# Revit family: Comfort-Height-WC-P-Round-With-Madison-Flushed-Lid-Tank-1
name_source: partatom
category: Plumbing Fixtures
units: mm (PartAtom-declared; Revit-internal decimal feet)

## family parameters
Always vertical = Yes
Cut with Voids When Loaded = No
OmniClass Number = 23.45.00.00
OmniClass Title = Sanitary, Laundry, and Cleaning Equipment
Part Type = Normal
Room Calculation Point = No
Round Connector Dimension = Use Diameter
Shared = No
Work Plane-Based = No

## types (2) — shared parameters
Flush rate = 3/6 L
Flush system/ Function = Siphon-jet Dual Flush system
Inlet Size = 13 mm
Manufacturer = HÄFELE (Thailand) Limited
Material = Ceramic White
Product Type = Two piece toilet
Product shape = Elongated
Seat cover info. = PP Soft Close System
Series = CIRINO
Standard/ code = TIS 792 : 2554
Trapway type = S-Trap rough-in 305 mm
URL = https://www.hafelethailand.com
zero-valued in all types: Default Elevation

## per-type parameters (varying)
| type | Height | Length | Outlet Size | Product code | SKU-1 | SKU-2 | Weight | Width |
| HAFELE Two piece toilet CIRINO 588.51.421 | 787 mm  [stored 2.58202 ft] | 766 mm  [stored 2.51312 ft] | 90 mm  [stored 0.295276 ft] | 588.51.421 | Yes | No | 35.64 | 384 mm  [stored 1.25984 ft] |
| HAFELE Two piece toilet CIRINO 588.51.401 | 810 mm | 745 mm  [stored 2.44423 ft] | 80 mm  [stored 0.262467 ft] | 588.51.401 | No | Yes | 40.02 | 356 mm  [stored 1.16798 ft] |

note: [stored X ft] marks values corroborated as IEEE doubles in the binary element streams (Revit-internal decimal feet)

## geometry (parser evidence)
native form markers: Sweep x2
no freeform markers — native parametric forms only
